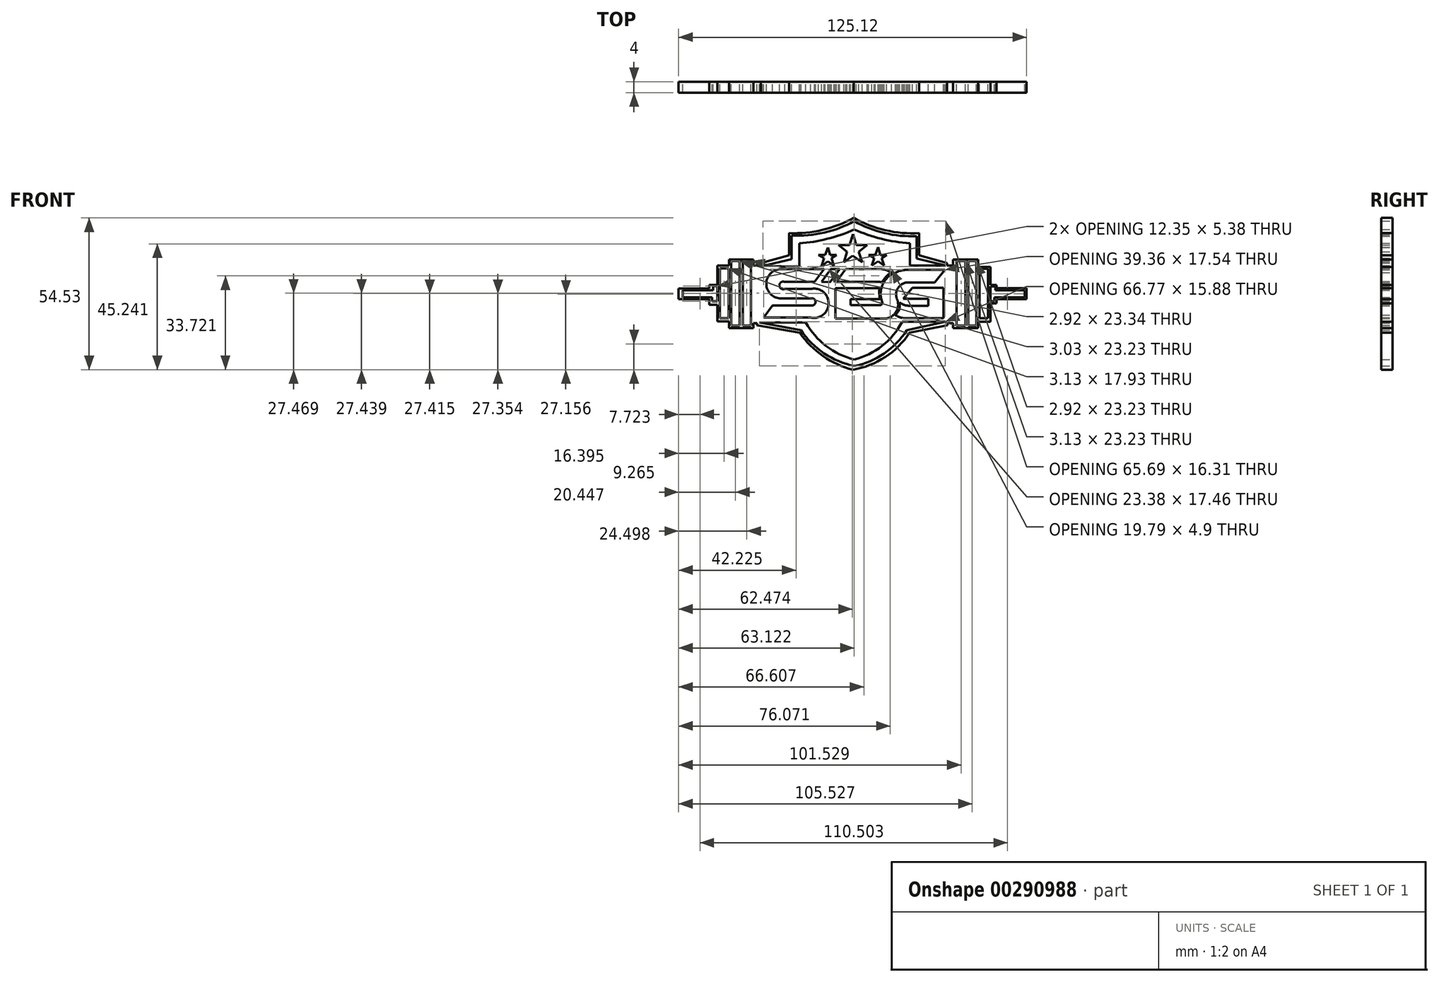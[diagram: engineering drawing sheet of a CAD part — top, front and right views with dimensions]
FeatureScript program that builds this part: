
annotation { "Feature Type Name" : "Feature", "Feature Type Description" : "" }
export const myFeature = defineFeature(function(context is Context, id is Id, definition is map)
    precondition{}
    {
        {
            var Q0;
            Q0=qCreatedBy(makeId("Front.planeOp"),FACE);
            var sketch = newSketch(context, id + "F0", { "sketchPlane" : qUnion([Q0])});
            skLineSegment(sketch, "E0", {"start": v(-28.73, 27.46) * mm, "end": v(-18.36, 29.84) * mm});
            skLineSegment(sketch, "E1", {"start": v(-18.36, 29.84) * mm, "end": v(-18.36, 38.37) * mm});
            skLineSegment(sketch, "E2", {"start": v(26.58, 38.16) * mm, "end": v(26.58, 30.16) * mm});
            skLineSegment(sketch, "E3", {"start": v(26.58, 30.16) * mm, "end": v(36.96, 27.57) * mm});
            skLineSegment(sketch, "E4", {"start": v(36.96, 27.57) * mm, "end": v(24.1, 27.57) * mm});
            skLineSegment(sketch, "E5", {"start": v(24.1, 27.57) * mm, "end": v(24.1, 35.56) * mm});
            skLineSegment(sketch, "E6", {"start": v(-15.66, 35.56) * mm, "end": v(-15.66, 27.24) * mm});
            skLineSegment(sketch, "E7", {"start": v(-15.66, 27.24) * mm, "end": v(-28.73, 27.46) * mm});
            skArc(sketch, "E8", {"start": v(-18.36, 38.37) * mm, "mid": v(-6.76, 39.4) * mm, "end": v(4.11, 43.56) * mm});
            skArc(sketch, "E9", {"start": v(4.11, 43.56) * mm, "mid": v(14.97, 39.29) * mm, "end": v(26.58, 38.16) * mm});
            skArc(sketch, "E10", {"start": v(-15.66, 35.56) * mm, "mid": v(-5.56, 37.2) * mm, "end": v(4.11, 40.53) * mm});
            skArc(sketch, "E11", {"start": v(4.11, 40.53) * mm, "mid": v(13.9, 37.21) * mm, "end": v(24.1, 35.56) * mm});
            skLineSegment(sketch, "E12", {"start": v(-29.92, 7.15) * mm, "end": v(-13.28, 7.15) * mm});
            skLineSegment(sketch, "E13", {"start": v(21.29, 7.37) * mm, "end": v(36.85, 7.37) * mm});
            skLineSegment(sketch, "E14", {"start": v(36.85, 7.37) * mm, "end": v(23.02, 4.34) * mm});
            skLineSegment(sketch, "E15", {"start": v(-15.01, 4.34) * mm, "end": v(-29.92, 7.15) * mm});
            skArc(sketch, "E16", {"start": v(-13.28, 7.15) * mm, "mid": v(-5.98, -1.32) * mm, "end": v(4.11, -6.14) * mm});
            skArc(sketch, "E17", {"start": v(4.11, -6.14) * mm, "mid": v(14.17, -1.26) * mm, "end": v(21.29, 7.37) * mm});
            skArc(sketch, "E18", {"start": v(4.11, -8.52) * mm, "mid": v(14.86, -4) * mm, "end": v(23.02, 4.34) * mm});
            skArc(sketch, "E19", {"start": v(-15.01, 4.34) * mm, "mid": v(-6.71, -3.97) * mm, "end": v(4.11, -8.52) * mm});
            skLineSegment(sketch, "E20.bottom", {"start": v(-35.97, 29.3) * mm, "end": v(-33.05, 29.3) * mm});
            skLineSegment(sketch, "E20.top", {"start": v(-35.97, 5.96) * mm, "end": v(-33.05, 5.96) * mm});
            skLineSegment(sketch, "E20.left", {"start": v(-35.97, 29.3) * mm, "end": v(-35.97, 5.96) * mm});
            skLineSegment(sketch, "E20.right", {"start": v(-33.05, 29.3) * mm, "end": v(-33.05, 5.96) * mm});
            skLineSegment(sketch, "E21.bottom", {"start": v(-40.08, 29.19) * mm, "end": v(-37.05, 29.19) * mm});
            skLineSegment(sketch, "E21.top", {"start": v(-40.08, 5.96) * mm, "end": v(-37.05, 5.96) * mm});
            skLineSegment(sketch, "E21.left", {"start": v(-40.08, 29.19) * mm, "end": v(-40.08, 5.96) * mm});
            skLineSegment(sketch, "E21.right", {"start": v(-37.05, 29.19) * mm, "end": v(-37.05, 5.96) * mm});
            skLineSegment(sketch, "E22.bottom", {"start": v(-44.18, 26.6) * mm, "end": v(-41.05, 26.6) * mm});
            skLineSegment(sketch, "E22.top", {"start": v(-44.18, 8.66) * mm, "end": v(-41.05, 8.66) * mm});
            skLineSegment(sketch, "E22.left", {"start": v(-44.18, 26.6) * mm, "end": v(-44.18, 8.66) * mm});
            skLineSegment(sketch, "E22.right", {"start": v(-41.05, 26.6) * mm, "end": v(-41.05, 8.66) * mm});
            skLineSegment(sketch, "E23.bottom", {"start": v(40.95, 29.19) * mm, "end": v(44.09, 29.19) * mm});
            skLineSegment(sketch, "E23.top", {"start": v(40.95, 5.96) * mm, "end": v(44.09, 5.96) * mm});
            skLineSegment(sketch, "E23.left", {"start": v(40.95, 29.19) * mm, "end": v(40.95, 5.96) * mm});
            skLineSegment(sketch, "E23.right", {"start": v(44.09, 29.19) * mm, "end": v(44.09, 5.96) * mm});
            skLineSegment(sketch, "E24.bottom", {"start": v(45.06, 29.19) * mm, "end": v(47.98, 29.19) * mm});
            skLineSegment(sketch, "E24.top", {"start": v(45.06, 5.96) * mm, "end": v(47.98, 5.96) * mm});
            skLineSegment(sketch, "E24.left", {"start": v(45.06, 29.19) * mm, "end": v(45.06, 5.96) * mm});
            skLineSegment(sketch, "E24.right", {"start": v(47.98, 29.19) * mm, "end": v(47.98, 5.96) * mm});
            skLineSegment(sketch, "E25.bottom", {"start": v(49.16, 26.49) * mm, "end": v(52.19, 26.49) * mm});
            skLineSegment(sketch, "E25.top", {"start": v(49.16, 8.66) * mm, "end": v(52.19, 8.66) * mm});
            skLineSegment(sketch, "E25.left", {"start": v(49.16, 26.49) * mm, "end": v(49.16, 8.66) * mm});
            skLineSegment(sketch, "E25.right", {"start": v(52.19, 26.49) * mm, "end": v(52.19, 8.66) * mm});
            skLineSegment(sketch, "E26", {"start": v(-45.11, 20.09) * mm, "end": v(-45.11, 14.82) * mm});
            skLineSegment(sketch, "E27", {"start": v(-45.11, 14.82) * mm, "end": v(-46.94, 14.82) * mm});
            skLineSegment(sketch, "E28", {"start": v(-46.94, 14.82) * mm, "end": v(-46.94, 16.2) * mm});
            skLineSegment(sketch, "E29", {"start": v(-46.94, 16.2) * mm, "end": v(-57.46, 16.2) * mm});
            skLineSegment(sketch, "E30", {"start": v(-57.46, 16.2) * mm, "end": v(-57.46, 18.72) * mm});
            skLineSegment(sketch, "E31", {"start": v(-57.46, 18.72) * mm, "end": v(-46.6, 18.72) * mm});
            skLineSegment(sketch, "E32", {"start": v(-46.6, 18.72) * mm, "end": v(-46.6, 20.2) * mm});
            skLineSegment(sketch, "E33", {"start": v(-46.6, 20.2) * mm, "end": v(-45.11, 20.09) * mm});
            skLineSegment(sketch, "E34", {"start": v(53.04, 14.85) * mm, "end": v(53.04, 20.12) * mm});
            skLineSegment(sketch, "E35", {"start": v(53.04, 20.12) * mm, "end": v(54.87, 20.12) * mm});
            skLineSegment(sketch, "E36", {"start": v(54.87, 20.12) * mm, "end": v(54.87, 18.74) * mm});
            skLineSegment(sketch, "E37", {"start": v(54.87, 18.74) * mm, "end": v(65.39, 18.74) * mm});
            skLineSegment(sketch, "E38", {"start": v(65.39, 18.74) * mm, "end": v(65.39, 16.22) * mm});
            skLineSegment(sketch, "E39", {"start": v(65.39, 16.22) * mm, "end": v(54.53, 16.22) * mm});
            skLineSegment(sketch, "E40", {"start": v(54.53, 16.22) * mm, "end": v(54.53, 14.74) * mm});
            skLineSegment(sketch, "E41", {"start": v(54.53, 14.74) * mm, "end": v(53.04, 14.85) * mm});
            skLineSegment(sketch, "E42", {"start": v(-8.71, 31.4) * mm, "end": v(-6.3, 31.4) * mm});
            skPoint(sketch, "E42.startSnap0", {"position": v(-15.66, 31.4) * mm});
            skLineSegment(sketch, "E43", {"start": v(-6.3, 31.4) * mm, "end": v(-5.28, 34.1) * mm});
            skLineSegment(sketch, "E44", {"start": v(-5.28, 34.1) * mm, "end": v(-4.56, 31.4) * mm});
            skLineSegment(sketch, "E45", {"start": v(-4.56, 31.4) * mm, "end": v(-2.22, 31.4) * mm});
            skLineSegment(sketch, "E46", {"start": v(-2.22, 31.4) * mm, "end": v(-4.06, 30.22) * mm});
            skLineSegment(sketch, "E47", {"start": v(-4.06, 30.22) * mm, "end": v(-3.2, 27.48) * mm});
            skLineSegment(sketch, "E48", {"start": v(-3.2, 27.48) * mm, "end": v(-5.28, 29.07) * mm});
            skLineSegment(sketch, "E49", {"start": v(-5.28, 29.07) * mm, "end": v(-7.63, 27.48) * mm});
            skLineSegment(sketch, "E50", {"start": v(-7.63, 27.48) * mm, "end": v(-6.76, 30.22) * mm});
            skLineSegment(sketch, "E51", {"start": v(-6.76, 30.22) * mm, "end": v(-8.71, 31.4) * mm});
            skLineSegment(sketch, "E52", {"start": v(3.55, 31.2) * mm, "end": v(0.34, 28.75) * mm});
            skLineSegment(sketch, "E53", {"start": v(0.34, 28.75) * mm, "end": v(1.57, 32.53) * mm});
            skLineSegment(sketch, "E54", {"start": v(1.57, 32.53) * mm, "end": v(-1.5, 34.99) * mm});
            skLineSegment(sketch, "E55", {"start": v(-1.5, 34.99) * mm, "end": v(2.47, 34.99) * mm});
            skLineSegment(sketch, "E56", {"start": v(2.47, 34.99) * mm, "end": v(3.75, 38.94) * mm});
            skLineSegment(sketch, "E57", {"start": v(3.75, 38.94) * mm, "end": v(4.85, 34.99) * mm});
            skLineSegment(sketch, "E58", {"start": v(4.85, 34.99) * mm, "end": v(8.75, 34.99) * mm});
            skLineSegment(sketch, "E59", {"start": v(8.75, 34.99) * mm, "end": v(5.72, 32.53) * mm});
            skLineSegment(sketch, "E60", {"start": v(5.72, 32.53) * mm, "end": v(7.02, 28.78) * mm});
            skLineSegment(sketch, "E61", {"start": v(7.02, 28.78) * mm, "end": v(3.55, 31.2) * mm});
            skLineSegment(sketch, "E62", {"start": v(9.32, 31.47) * mm, "end": v(11.72, 31.47) * mm});
            skLineSegment(sketch, "E63", {"start": v(11.72, 31.47) * mm, "end": v(12.75, 34.16) * mm});
            skLineSegment(sketch, "E64", {"start": v(12.75, 34.16) * mm, "end": v(13.46, 31.47) * mm});
            skLineSegment(sketch, "E65", {"start": v(13.46, 31.47) * mm, "end": v(15.8, 31.47) * mm});
            skLineSegment(sketch, "E66", {"start": v(15.8, 31.47) * mm, "end": v(13.97, 30.29) * mm});
            skLineSegment(sketch, "E67", {"start": v(13.97, 30.29) * mm, "end": v(14.83, 27.55) * mm});
            skLineSegment(sketch, "E68", {"start": v(14.83, 27.55) * mm, "end": v(12.75, 29.13) * mm});
            skLineSegment(sketch, "E69", {"start": v(12.75, 29.13) * mm, "end": v(10.4, 27.55) * mm});
            skLineSegment(sketch, "E70", {"start": v(10.4, 27.55) * mm, "end": v(11.27, 30.29) * mm});
            skLineSegment(sketch, "E71", {"start": v(11.27, 30.29) * mm, "end": v(9.32, 31.47) * mm});
            skLineSegment(sketch, "E72", {"start": v(-6.76, 26.33) * mm, "end": v(-22.2, 26.33) * mm});
            skPoint(sketch, "E72.endSnap0", {"position": v(-22.2, 27.35) * mm});
            skArc(sketch, "E73", {"start": v(-22.2, 26.33) * mm, "mid": v(-27.47, 21.05) * mm, "end": v(-22.2, 15.78) * mm});
            skLineSegment(sketch, "E74", {"start": v(-22.2, 15.78) * mm, "end": v(-11.5, 15.78) * mm});
            skLineSegment(sketch, "E75", {"start": v(-11.5, 13.26) * mm, "end": v(-25.22, 13.26) * mm});
            skLineSegment(sketch, "E76", {"start": v(-25.22, 13.26) * mm, "end": v(-28.48, 8.87) * mm});
            skLineSegment(sketch, "E77", {"start": v(-28.48, 8.87) * mm, "end": v(-11.5, 8.87) * mm});
            skLineSegment(sketch, "E78", {"start": v(-11.5, 19.2) * mm, "end": v(-20.87, 19.2) * mm});
            skLineSegment(sketch, "E79", {"start": v(-20.87, 21.72) * mm, "end": v(-10.1, 21.72) * mm});
            skLineSegment(sketch, "E80", {"start": v(-10.1, 21.72) * mm, "end": v(-6.76, 26.33) * mm});
            skArc(sketch, "E81", {"start": v(-20.87, 21.72) * mm, "mid": v(-22.78, 20.46) * mm, "end": v(-20.87, 19.2) * mm});
            skArc(sketch, "E82", {"start": v(-11.5, 13.26) * mm, "mid": v(-9.8, 14.52) * mm, "end": v(-11.5, 15.78) * mm});
            skArc(sketch, "E83", {"start": v(-11.5, 8.87) * mm, "mid": v(-5.1, 14.04) * mm, "end": v(-11.5, 19.2) * mm});
            skLineSegment(sketch, "E84", {"start": v(-4.24, 26.33) * mm, "end": v(-7.59, 21.72) * mm});
            skLineSegment(sketch, "E85", {"start": v(-7.59, 21.72) * mm, "end": v(-4.52, 21.67) * mm});
            skLineSegment(sketch, "E86", {"start": v(-4.52, 21.67) * mm, "end": v(-1.14, 26.33) * mm});
            skLineSegment(sketch, "E87", {"start": v(-1.14, 26.33) * mm, "end": v(-4.24, 26.33) * mm});
            skLineSegment(sketch, "E88", {"start": v(1.04, 26.33) * mm, "end": v(-2.3, 21.72) * mm});
            skLineSegment(sketch, "E89", {"start": v(-2.3, 21.72) * mm, "end": v(13.27, 21.72) * mm});
            skLineSegment(sketch, "E90", {"start": v(13.34, 26.33) * mm, "end": v(1.04, 26.33) * mm});
            skArc(sketch, "E91", {"start": v(17.5, 25.08) * mm, "mid": v(15.5, 26) * mm, "end": v(13.34, 26.33) * mm});
            skArc(sketch, "E92", {"start": v(17.5, 25.08) * mm, "mid": v(15.5, 23.52) * mm, "end": v(14.07, 21.43) * mm});
            skArc(sketch, "E93", {"start": v(14.07, 21.43) * mm, "mid": v(13.7, 21.65) * mm, "end": v(13.27, 21.72) * mm});
            skLineSegment(sketch, "E94", {"start": v(13.2, 19.4) * mm, "end": v(-2.62, 19.42) * mm});
            skLineSegment(sketch, "E95", {"start": v(-2.62, 19.42) * mm, "end": v(-2.62, 8.55) * mm});
            skLineSegment(sketch, "E96", {"start": v(-2.62, 8.55) * mm, "end": v(14.93, 8.55) * mm});
            skArc(sketch, "E97", {"start": v(14.93, 8.55) * mm, "mid": v(18.63, 10.2) * mm, "end": v(19.88, 14.06) * mm});
            skArc(sketch, "E98", {"start": v(19.88, 14.06) * mm, "mid": v(19.71, 14.96) * mm, "end": v(19.37, 15.8) * mm});
            skArc(sketch, "E99", {"start": v(22.88, 21.5) * mm, "mid": v(19.83, 19.45) * mm, "end": v(19.37, 15.8) * mm});
            skArc(sketch, "E100", {"start": v(13.2, 19.4) * mm, "mid": v(13.15, 17.46) * mm, "end": v(13.34, 15.52) * mm});
            skLineSegment(sketch, "E101", {"start": v(13.34, 15.52) * mm, "end": v(2.81, 15.53) * mm});
            skLineSegment(sketch, "E102", {"start": v(2.81, 15.53) * mm, "end": v(2.81, 13.36) * mm});
            skLineSegment(sketch, "E103", {"start": v(2.81, 13.36) * mm, "end": v(13.34, 13.35) * mm});
            skArc(sketch, "E104", {"start": v(13.34, 13.35) * mm, "mid": v(13.98, 13.62) * mm, "end": v(14.24, 14.27) * mm});
            skArc(sketch, "E105", {"start": v(14.47, 20.95) * mm, "mid": v(13.63, 17.64) * mm, "end": v(14.24, 14.27) * mm});
            skArc(sketch, "E106", {"start": v(19, 25.1) * mm, "mid": v(16.3, 23.5) * mm, "end": v(14.47, 20.95) * mm});
            skArc(sketch, "E107", {"start": v(23.6, 26.09) * mm, "mid": v(21.25, 25.86) * mm, "end": v(19, 25.1) * mm});
            skLineSegment(sketch, "E108", {"start": v(23.6, 26.09) * mm, "end": v(36.74, 26.09) * mm});
            skLineSegment(sketch, "E109", {"start": v(36.74, 26.09) * mm, "end": v(33.05, 21.53) * mm});
            skLineSegment(sketch, "E110", {"start": v(33.05, 21.53) * mm, "end": v(22.88, 21.5) * mm});
            skArc(sketch, "E111", {"start": v(18.92, 9.85) * mm, "mid": v(20.3, 11.94) * mm, "end": v(20.4, 14.44) * mm});
            skArc(sketch, "E112", {"start": v(18.92, 9.85) * mm, "mid": v(20.48, 9.02) * mm, "end": v(22.22, 8.67) * mm});
            skArc(sketch, "E113", {"start": v(20.4, 14.44) * mm, "mid": v(21.83, 13.56) * mm, "end": v(23.46, 13.17) * mm});
            skLineSegment(sketch, "E114", {"start": v(23.46, 13.17) * mm, "end": v(30.7, 13.17) * mm});
            skLineSegment(sketch, "E115", {"start": v(30.7, 13.17) * mm, "end": v(30.7, 15.64) * mm});
            skLineSegment(sketch, "E116", {"start": v(30.7, 15.64) * mm, "end": v(21.79, 15.64) * mm});
            skLineSegment(sketch, "E117", {"start": v(21.79, 15.64) * mm, "end": v(25.08, 19.6) * mm});
            skLineSegment(sketch, "E118", {"start": v(25.08, 19.6) * mm, "end": v(36.27, 19.6) * mm});
            skLineSegment(sketch, "E119", {"start": v(36.27, 19.6) * mm, "end": v(36.27, 8.67) * mm});
            skLineSegment(sketch, "E120", {"start": v(36.27, 8.67) * mm, "end": v(22.22, 8.67) * mm});
            skSolve(sketch);
        }
        {
            var Q0;
            Q0=qCreatedBy(makeId("Front.planeOp"),FACE);
            var sketch = newSketch(context, id + "F1", { "sketchPlane" : qUnion([Q0])});
            skLineSegment(sketch, "E121", {"start": v(-59.01, 15.48) * mm, "end": v(-47.98, 15.48) * mm});
            skLineSegment(sketch, "E122", {"start": v(-47.98, 15.48) * mm, "end": v(-47.98, 13.54) * mm});
            skLineSegment(sketch, "E123", {"start": v(-47.98, 13.54) * mm, "end": v(-45.1, 13.54) * mm});
            skLineSegment(sketch, "E124", {"start": v(-45.1, 13.54) * mm, "end": v(-45.1, 7.56) * mm});
            skLineSegment(sketch, "E125", {"start": v(-45.1, 7.56) * mm, "end": v(-40.84, 7.56) * mm});
            skLineSegment(sketch, "E126", {"start": v(-40.84, 7.56) * mm, "end": v(-40.84, 5.07) * mm});
            skLineSegment(sketch, "E127", {"start": v(-40.84, 5.07) * mm, "end": v(-32.14, 5.07) * mm});
            skLineSegment(sketch, "E128", {"start": v(-32.14, 5.07) * mm, "end": v(-32.14, 6.93) * mm});
            skLineSegment(sketch, "E129", {"start": v(-32.14, 6.93) * mm, "end": v(-30.9, 6.93) * mm});
            skLineSegment(sketch, "E130", {"start": v(-30.9, 6.93) * mm, "end": v(-30.9, 6.16) * mm});
            skLineSegment(sketch, "E131", {"start": v(-30.9, 6.16) * mm, "end": v(-15.44, 3.44) * mm});
            skArc(sketch, "E132", {"start": v(-15.44, 3.44) * mm, "mid": v(-7.1, -4.95) * mm, "end": v(3.69, -9.84) * mm});
            skArc(sketch, "E133", {"start": v(3.69, -9.84) * mm, "mid": v(15.24, -5.29) * mm, "end": v(24.07, 3.44) * mm});
            skLineSegment(sketch, "E134", {"start": v(24.07, 3.44) * mm, "end": v(37.57, 6.16) * mm});
            skLineSegment(sketch, "E135", {"start": v(37.57, 6.16) * mm, "end": v(37.7, 6.93) * mm});
            skLineSegment(sketch, "E136", {"start": v(37.7, 6.93) * mm, "end": v(39.64, 6.93) * mm});
            skLineSegment(sketch, "E137", {"start": v(39.64, 6.93) * mm, "end": v(39.64, 5.07) * mm});
            skLineSegment(sketch, "E138", {"start": v(39.64, 5.07) * mm, "end": v(48.67, 5.07) * mm});
            skLineSegment(sketch, "E139", {"start": v(48.67, 5.07) * mm, "end": v(48.67, 7.47) * mm});
            skLineSegment(sketch, "E140", {"start": v(48.67, 7.47) * mm, "end": v(53.09, 7.47) * mm});
            skLineSegment(sketch, "E141", {"start": v(53.09, 7.47) * mm, "end": v(53.09, 14.07) * mm});
            skLineSegment(sketch, "E142", {"start": v(53.09, 14.07) * mm, "end": v(55.3, 14.07) * mm});
            skLineSegment(sketch, "E143", {"start": v(55.3, 14.07) * mm, "end": v(55.3, 15.57) * mm});
            skLineSegment(sketch, "E144", {"start": v(55.3, 15.57) * mm, "end": v(66.1, 15.57) * mm});
            skLineSegment(sketch, "E145", {"start": v(66.1, 15.57) * mm, "end": v(66.1, 19.5) * mm});
            skLineSegment(sketch, "E146", {"start": v(66.1, 19.5) * mm, "end": v(55.3, 19.5) * mm});
            skLineSegment(sketch, "E147", {"start": v(55.3, 19.5) * mm, "end": v(55.3, 20.64) * mm});
            skLineSegment(sketch, "E148", {"start": v(55.3, 20.64) * mm, "end": v(53.09, 20.64) * mm});
            skLineSegment(sketch, "E149", {"start": v(53.09, 20.64) * mm, "end": v(53.09, 27.12) * mm});
            skLineSegment(sketch, "E150", {"start": v(53.09, 27.12) * mm, "end": v(48.67, 27.12) * mm});
            skLineSegment(sketch, "E151", {"start": v(48.67, 27.12) * mm, "end": v(48.67, 29.82) * mm});
            skLineSegment(sketch, "E152", {"start": v(48.67, 29.82) * mm, "end": v(39.62, 29.82) * mm});
            skLineSegment(sketch, "E153", {"start": v(39.62, 29.82) * mm, "end": v(39.62, 27.58) * mm});
            skLineSegment(sketch, "E154", {"start": v(39.62, 27.58) * mm, "end": v(37.44, 27.58) * mm});
            skLineSegment(sketch, "E155", {"start": v(37.44, 27.58) * mm, "end": v(37.44, 28.46) * mm});
            skLineSegment(sketch, "E156", {"start": v(37.44, 28.46) * mm, "end": v(27.43, 31.26) * mm});
            skLineSegment(sketch, "E157", {"start": v(27.43, 31.26) * mm, "end": v(27.43, 39.23) * mm});
            skArc(sketch, "E158", {"start": v(3.92, 44.7) * mm, "mid": v(15.29, 40.3) * mm, "end": v(27.43, 39.23) * mm});
            skArc(sketch, "E159", {"start": v(-19.3, 39.23) * mm, "mid": v(-7.32, 40.4) * mm, "end": v(3.92, 44.7) * mm});
            skLineSegment(sketch, "E160", {"start": v(-19.3, 39.23) * mm, "end": v(-19.3, 31.26) * mm});
            skLineSegment(sketch, "E161", {"start": v(-19.3, 31.26) * mm, "end": v(-29.4, 28.46) * mm});
            skLineSegment(sketch, "E162", {"start": v(-29.4, 28.46) * mm, "end": v(-29.4, 27.58) * mm});
            skLineSegment(sketch, "E163", {"start": v(-29.4, 27.58) * mm, "end": v(-32.14, 27.58) * mm});
            skLineSegment(sketch, "E164", {"start": v(-32.14, 27.58) * mm, "end": v(-32.14, 29.82) * mm});
            skLineSegment(sketch, "E165", {"start": v(-32.14, 29.82) * mm, "end": v(-40.84, 29.82) * mm});
            skLineSegment(sketch, "E166", {"start": v(-40.84, 29.82) * mm, "end": v(-40.84, 27.58) * mm});
            skLineSegment(sketch, "E167", {"start": v(-40.84, 27.58) * mm, "end": v(-45.1, 27.58) * mm});
            skLineSegment(sketch, "E168", {"start": v(-45.1, 27.58) * mm, "end": v(-45.1, 20.64) * mm});
            skLineSegment(sketch, "E169", {"start": v(-45.1, 20.64) * mm, "end": v(-47.98, 20.64) * mm});
            skLineSegment(sketch, "E170", {"start": v(-47.98, 20.64) * mm, "end": v(-47.98, 19.4) * mm});
            skLineSegment(sketch, "E171", {"start": v(-47.98, 19.4) * mm, "end": v(-59.01, 19.4) * mm});
            skLineSegment(sketch, "E172", {"start": v(-59.01, 19.4) * mm, "end": v(-59.01, 15.48) * mm});
            skSolve(sketch);
        }
        {
            var Q0;
            Q0 = qSketchRegion(id + "F1", true);
            extrude(context, id + "F2", {"entities" : qUnion([Q0]), "depth" : 4 * mm});
        }
        {
            var Q0;
            Q0 = qSketchRegion(id + "F0", true);
            extrude(context, id + "F3", {"entities" : qUnion([Q0]), "operationType" : NewBodyOperationType.REMOVE, "depth" : 25 * mm});
        }
    });
